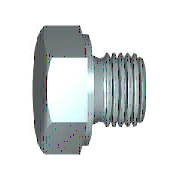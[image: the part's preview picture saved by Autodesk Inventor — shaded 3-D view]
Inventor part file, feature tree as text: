
AUTODESK INVENTOR PART (.ipt)
format: ipt  version: 2025 (Build 290162000, 162)  size: 195,072 bytes
history: native  units: mm (DEFAULTED — no unit token found)
features: other x3, extrude x1, chamfer x1, plane x1
ambient origin geometry x8: Origin, YZ Plane, XZ Plane, XY Plane, X Axis, Y Axis, Z Axis, Center Point
bodies: Solid1 (feature_tree)
feature tree (6):
  other  "轴承体"
  extrude  "头"  Depth=16.0mm
  other  "沟槽1"
  chamfer  "倒角2"  Distance=10.0mm
  other  "Work Axis1"
  plane  "Work Plane1"
